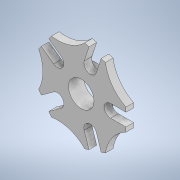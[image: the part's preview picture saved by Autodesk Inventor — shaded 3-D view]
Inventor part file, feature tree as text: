
AUTODESK INVENTOR PART (.ipt)
format: ipt  version: 2022 (Build 260153000, 153)  size: 176,640 bytes
history: native  units: mm
features: extrude x2, other x1, sketch x1
ambient origin geometry x8: Origin, YZ Plane, XZ Plane, XY Plane, X Axis, Y Axis, Z Axis, Center Point
bodies: Body1 (feature_tree)
feature tree (4):
  other  "Sólido1"
  sketch  "Esboço1"  dims[d0=20.0mm d1=30.0mm d2=5.0mm d3=23.0mm d4=60.0mm d5=60.0mm d6=35.0mm d7=100.0mm d8=100.0mm d9=150.0mm d10=5.0mm d11=62.73131mm d12=50.0mm d14=360.0deg d16=6.0mm d17=0.0mm d18=12.0mm d19=0.0mm]
  extrude  "Extrusão1"  Depth=30.0mm
  extrude  "Extrusão2"  Depth=5.0mm
